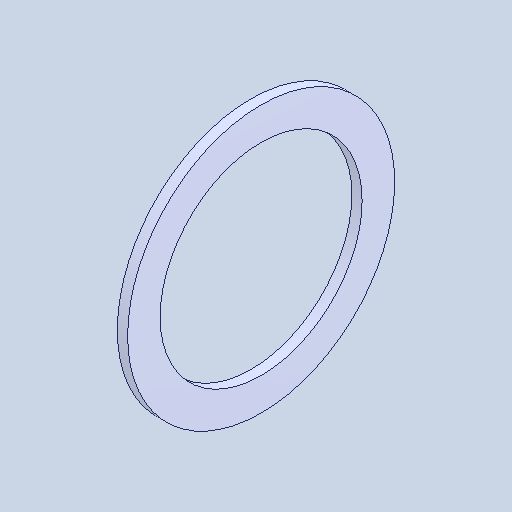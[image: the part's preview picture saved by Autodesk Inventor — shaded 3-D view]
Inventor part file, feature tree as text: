
AUTODESK INVENTOR PART (.ipt)
format: ipt  version: 2024.1 (Build 281209000, 209)  size: 89,600 bytes
history: native  units: in
note: dims shown in document units (in); Inventor stores cm internally (conversion verified against a paired STEP export)
features: revolve x1
ambient origin geometry x8: Origin, YZ Plane, XZ Plane, XY Plane, X Axis, Y Axis, Z Axis, Center Point
bodies: Solid1 (feature_tree)
feature tree (1):
  revolve  "Revolve1"  [1 undecoded]
note: 1 required parameter value undecoded (feature->parameter linkage not recoverable at this tier; creation-order binding heuristic only, values carry confidence <= 0.55)
